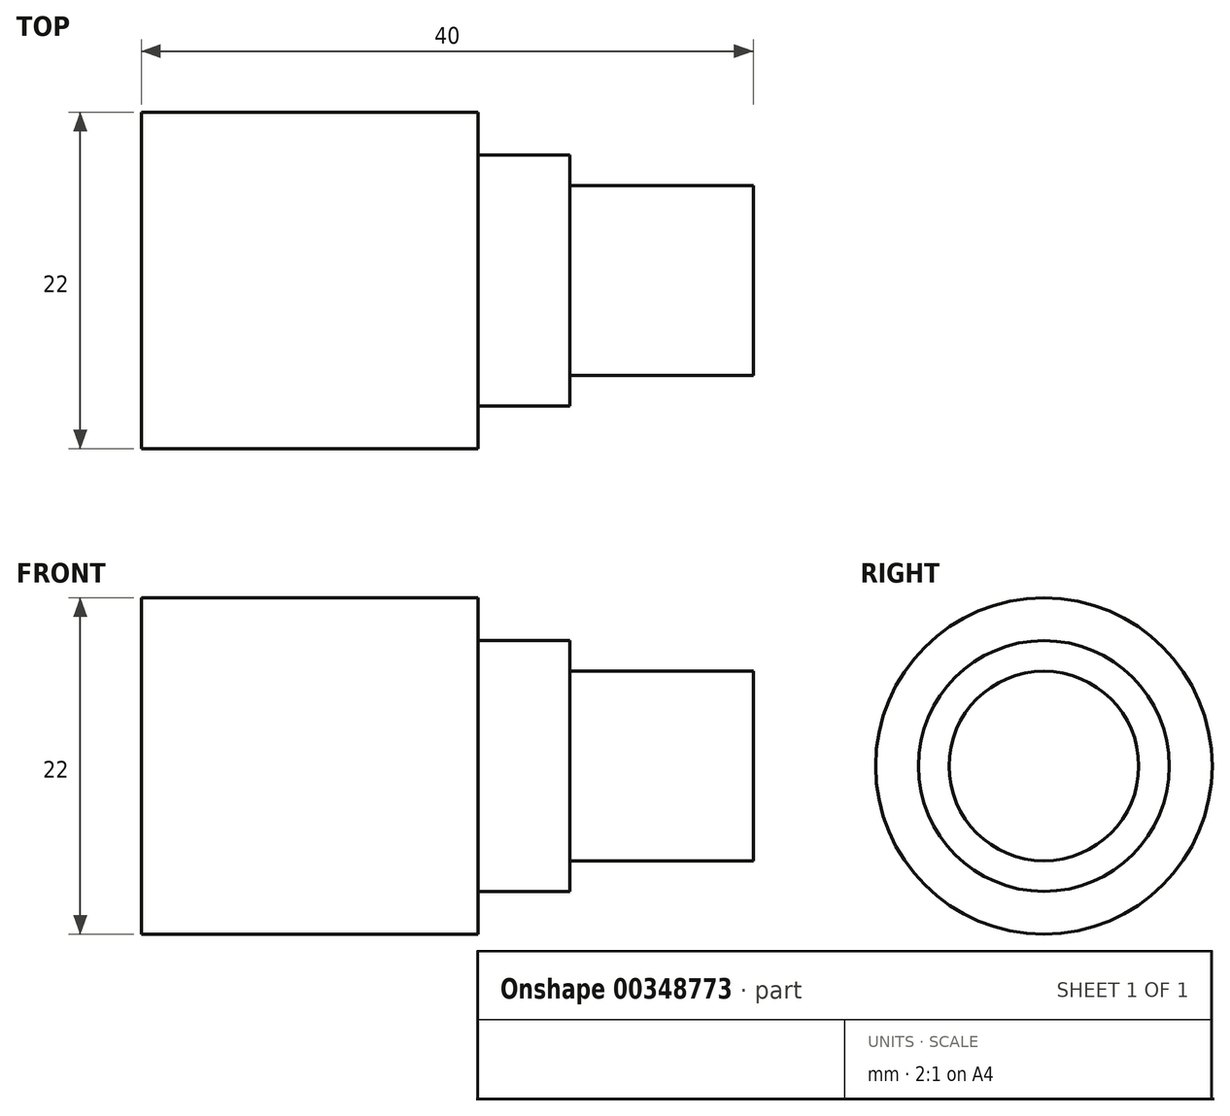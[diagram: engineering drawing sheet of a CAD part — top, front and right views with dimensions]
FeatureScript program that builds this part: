
annotation { "Feature Type Name" : "Feature", "Feature Type Description" : "" }
export const myFeature = defineFeature(function(context is Context, id is Id, definition is map)
    precondition{}
    {
        {
            var Q0;
            Q0=qCreatedBy(makeId("Top.planeOp"),FACE);
            var sketch = newSketch(context, id + "F0", { "sketchPlane" : qUnion([Q0])});
            skLineSegment(sketch, "E0", {"start": v(0, 0) * mm, "end": v(18, 0) * mm, "construction": true});
            skLineSegment(sketch, "E1", {"start": v(18, 0) * mm, "end": v(6, 0) * mm});
            skLineSegment(sketch, "E2", {"start": v(18, 0) * mm, "end": v(-22, 0) * mm, "construction": true});
            skSolve(sketch);
        }
        {
            var Q0;
            Q0=qCreatedBy(makeId("Right.planeOp"),FACE);
            var sketch = newSketch(context, id + "F1", { "sketchPlane" : qUnion([Q0])});
            skCircle(sketch, "E3", {"center": v(0, 0) * mm, "radius": 11 * mm});
            skCircle(sketch, "E4", {"center": v(0, 0) * mm, "radius": 8.2 * mm});
            skCircle(sketch, "E5", {"center": v(0, 0) * mm, "radius": 6.2 * mm});
            skSolve(sketch);
        }
        {
            var Q0;
            Q0 = qSketchRegion(id + "F1", true);
            var Q1;
            Q1=makeQuery(id+"F1.imprint","IMPRINT",FACE,{"disambiguationData":[TD([[makeQuery(id+"F1.imprint","IMPRINT",EDGE,{"derivedFrom":sQuery(id+"F1.wireOp",EDGE,"E5")}),1.0]])]});
            var Q2;
            Q2=makeQuery(id+"F1.imprint","IMPRINT",FACE,{"disambiguationData":[TD([[makeQuery(id+"F1.imprint","IMPRINT",EDGE,{"derivedFrom":sQuery(id+"F1.wireOp",EDGE,"E4")}),1.0]])]});
            var Q3;
            Q3=sQuery(id+"F0.wireOp",VERTEX,"E2.end");
            extrude(context, id + "F2", {"entities" : qUnion([Q0, Q1, Q2]), "endBound" : BoundingType.UP_TO_VERTEX, "oppositeDirection" : true, "endBoundEntityVertex" : qUnion([Q3]), "depth" : 25 * mm});
        }
        {
            var Q0;
            Q0=makeQuery(id+"F1.imprint","IMPRINT",FACE,{"disambiguationData":[TD([[makeQuery(id+"F1.imprint","IMPRINT",EDGE,{"derivedFrom":sQuery(id+"F1.wireOp",EDGE,"E5")}),1.0]])]});
            var Q1;
            Q1=sQuery(id+"F0.wireOp",VERTEX,"E2.start");
            extrude(context, id + "F3", {"entities" : qUnion([Q0]), "operationType" : NewBodyOperationType.ADD, "endBound" : BoundingType.UP_TO_VERTEX, "endBoundEntityVertex" : qUnion([Q1]), "depth" : 25 * mm});
        }
        {
            var Q0;
            Q0=makeQuery(id+"F1.imprint","IMPRINT",FACE,{"disambiguationData":[TD([[makeQuery(id+"F1.imprint","IMPRINT",EDGE,{"derivedFrom":sQuery(id+"F1.wireOp",EDGE,"E4")}),1.0]])]});
            var Q1;
            Q1=sQuery(id+"F0.wireOp",VERTEX,"E1.end");
            extrude(context, id + "F4", {"entities" : qUnion([Q0]), "operationType" : NewBodyOperationType.ADD, "endBound" : BoundingType.UP_TO_VERTEX, "endBoundEntityVertex" : qUnion([Q1]), "depth" : 25 * mm});
        }
        {
            var Q0;
            Q0=makeQuery(id+"F2.opExtrude","SWEPT_BODY",BODY,{"disambiguationData":[OSD([sQuery(id+"F1.wireOp",EDGE,"E3")])]});
            transform(context, id + "F5", {"entities" : qUnion([Q0]), "transformType" : TransformType.TRANSLATION_3D, "dx" : 22 * mm, "dy" : 0 * mm, "dz" : 0 * mm, "makeCopy" : false});
        }
    });
